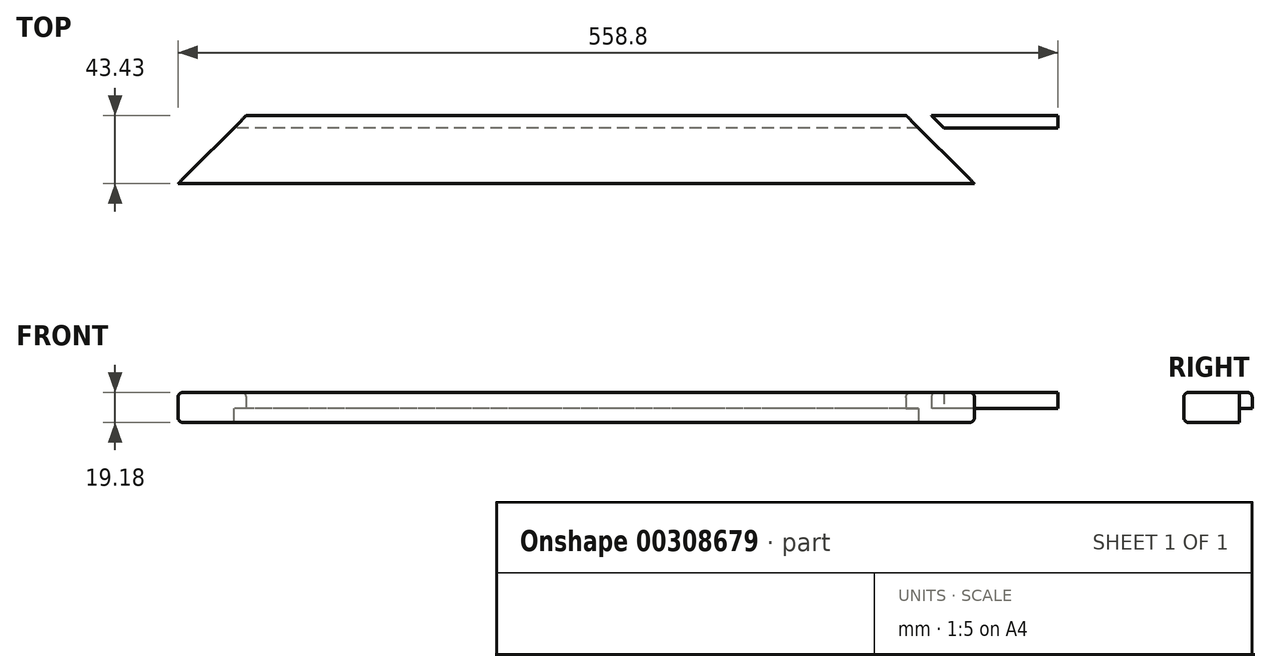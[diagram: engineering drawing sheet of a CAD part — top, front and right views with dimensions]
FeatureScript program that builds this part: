
annotation { "Feature Type Name" : "Feature", "Feature Type Description" : "" }
export const myFeature = defineFeature(function(context is Context, id is Id, definition is map)
    precondition{}
    {
        {
            var Q0;
            Q0=qCreatedBy(makeId("Right.planeOp"),FACE);
            var sketch = newSketch(context, id + "F0", { "sketchPlane" : qUnion([Q0])});
            skLineSegment(sketch, "E0.bottom", {"start": v(-48.17, 35.19) * mm, "end": v(-11.09, 35.19) * mm});
            skLineSegment(sketch, "E0.top", {"start": v(-48.17, 16) * mm, "end": v(-15.91, 16) * mm});
            skLineSegment(sketch, "E0.left", {"start": v(-51.34, 32.01) * mm, "end": v(-51.34, 19.18) * mm});
            skLineSegment(sketch, "E0.right", {"start": v(-7.91, 32.01) * mm, "end": v(-7.91, 24.9) * mm});
            skPoint(sketch, "E1.visualSharp", {"position": v(-51.34, 35.19) * mm});
            skArc(sketch, "E1.filletArc", {"start": v(-48.17, 35.19) * mm, "mid": v(-50.41, 34.26) * mm, "end": v(-51.34, 32.01) * mm});
            skPoint(sketch, "E2.visualSharp", {"position": v(-51.34, 16) * mm});
            skArc(sketch, "E2.filletArc", {"start": v(-51.34, 19.18) * mm, "mid": v(-50.41, 16.94) * mm, "end": v(-48.17, 16) * mm});
            skPoint(sketch, "E3.visualSharp", {"position": v(-7.91, 35.19) * mm});
            skArc(sketch, "E3.filletArc", {"start": v(-7.91, 32.01) * mm, "mid": v(-8.84, 34.26) * mm, "end": v(-11.09, 35.19) * mm});
            skLineSegment(sketch, "E4", {"start": v(-15.91, 24.9) * mm, "end": v(-15.91, 16) * mm});
            skLineSegment(sketch, "E5", {"start": v(-7.91, 24.9) * mm, "end": v(-15.91, 24.9) * mm});
            skSolve(sketch);
        }
        {
            var Q0;
            Q0=makeQuery(id+"F0.imprint","IMPRINT",FACE,{"disambiguationData":[TD([[makeQuery(id+"F0.imprint","IMPRINT",EDGE,{"derivedFrom":sQuery(id+"F0.wireOp",EDGE,"E0.bottom")}),-1.0]])]});
            extrude(context, id + "F1", {"entities" : qUnion([Q0]), "depth" : 558.8 * mm});
        }
        {
            var Q0;
            Q0=makeQuery(id+"F1.opExtrude","SWEPT_FACE",FACE,{"disambiguationData":[OSD([sQuery(id+"F0.wireOp",EDGE,"E0.bottom")])]});
            var sketch = newSketch(context, id + "F2", { "sketchPlane" : qUnion([Q0])});
            skLineSegment(sketch, "E6.0", {"start": v(558.8, -51.34) * mm, "end": v(0, -51.34) * mm});
            skLineSegment(sketch, "E7", {"start": v(0, -51.34) * mm, "end": v(43.43, -7.91) * mm});
            skLineSegment(sketch, "E8.0", {"start": v(558.8, -7.91) * mm, "end": v(0, -7.91) * mm});
            skLineSegment(sketch, "E9", {"start": v(0, -51.34) * mm, "end": v(0, -7.91) * mm});
            skSolve(sketch);
        }
        {
            var Q0;
            {var subQ0=sQuery(id+"F2.wireOp",EDGE,"E8.0");var subQ1=sQuery(id+"F2.wireOp",EDGE,"E7");var subQ2=makeQuery(id+"F2.imprint","INTERSECT",VERTEX,{"derivedFrom":[subQ1,subQ0]});Q0=makeQuery(id+"F2.imprint","IMPRINT",FACE,{"disambiguationData":[TD([[makeQuery(id+"F2.imprint","IMPRINT",EDGE,{"disambiguationData":[TD([[subQ2,-1.0]])],"derivedFrom":subQ0}),1.0]])]});}
            var Q1;
            {var subQ0=sQuery(id+"F2.wireOp",EDGE,"E7");var subQ1=sQuery(id+"F0.wireOp",EDGE,"E0.bottom");var subQ2=makeQuery(id+"F1.opExtrude","SWEPT_EDGE",EDGE,{"disambiguationData":[OSD([subQ1,sQuery(id+"F0.wireOp",EDGE,"E1.filletArc")])]});var subQ3=makeQuery(id+"F2.imprint","INTERSECT",VERTEX,{"derivedFrom":[subQ2,subQ0]});Q1=makeQuery(id+"F2.imprint","IMPRINT",FACE,{"disambiguationData":[TD([[makeQuery(id+"F2.imprint","IMPRINT",EDGE,{"disambiguationData":[TD([[subQ3,-1.0]])],"derivedFrom":subQ0}),1.0]])]});}
            var Q2;
            {var subQ0=sQuery(id+"F2.wireOp",EDGE,"E9");var subQ1=sQuery(id+"F2.wireOp",EDGE,"E7");var subQ2=makeQuery(id+"F2.imprint","INTERSECT",VERTEX,{"derivedFrom":[subQ1,subQ0]});Q2=makeQuery(id+"F2.imprint","IMPRINT",FACE,{"disambiguationData":[TD([[makeQuery(id+"F2.imprint","IMPRINT",EDGE,{"disambiguationData":[TD([[subQ2,-1.0]])],"derivedFrom":subQ1}),1.0]])]});}
            extrude(context, id + "F3", {"entities" : qUnion([Q0, Q1, Q2]), "operationType" : NewBodyOperationType.REMOVE, "endBound" : BoundingType.THROUGH_ALL, "oppositeDirection" : true, "depth" : 25.4 * mm});
        }
        {
            var Q0;
            Q0=makeQuery(id+"F1.opExtrude","SWEPT_FACE",FACE,{"disambiguationData":[OSD([sQuery(id+"F0.wireOp",EDGE,"E0.top")])]});
            var sketch = newSketch(context, id + "F4", { "sketchPlane" : qUnion([Q0])});
            skLineSegment(sketch, "E10.0", {"start": v(558.8, 51.34) * mm, "end": v(0, 51.34) * mm});
            skLineSegment(sketch, "E11.0", {"start": v(558.8, 7.91) * mm, "end": v(43.43, 7.91) * mm});
            skLineSegment(sketch, "E12", {"start": v(478.4, 51.34) * mm, "end": v(478.4, -40.2) * mm});
            skLineSegment(sketch, "E13", {"start": v(478.4, 7.91) * mm, "end": v(521.84, 51.34) * mm});
            skLineSegment(sketch, "E14.0", {"start": v(558.8, 48.17) * mm, "end": v(558.8, 15.91) * mm});
            skPoint(sketch, "E15.0", {"position": v(558.8, 50.41) * mm});
            skLineSegment(sketch, "E16.0", {"start": v(558.8, 7.91) * mm, "end": v(558.8, 15.91) * mm});
            skLineSegment(sketch, "E17", {"start": v(521.84, 51.34) * mm, "end": v(558.8, 51.34) * mm});
            skLineSegment(sketch, "E18", {"start": v(558.8, 7.91) * mm, "end": v(478.4, 7.91) * mm});
            skLineSegment(sketch, "E19", {"start": v(558.8, 51.34) * mm, "end": v(558.8, 7.91) * mm});
            skLineSegment(sketch, "E20.0", {"start": v(558.8, 15.91) * mm, "end": v(35.43, 15.91) * mm});
            skLineSegment(sketch, "E21", {"start": v(35.43, 15.91) * mm, "end": v(35.43, -67.97) * mm});
            skSolve(sketch);
        }
        {
            var Q0;
            {var subQ0=sQuery(id+"F4.wireOp",EDGE,"E17");Q0=makeQuery(id+"F4.imprint","IMPRINT",FACE,{"disambiguationData":[TD([[makeQuery(id+"F4.imprint","IMPRINT",EDGE,{"derivedFrom":subQ0}),-1.0]])]});}
            var Q1;
            {var subQ0=sQuery(id+"F4.wireOp",EDGE,"E13");var subQ1=sQuery(id+"F0.wireOp",EDGE,"E0.top");var subQ2=makeQuery(id+"F1.opExtrude","SWEPT_EDGE",EDGE,{"disambiguationData":[OSD([subQ1,sQuery(id+"F0.wireOp",EDGE,"E4")])]});var subQ3=makeQuery(id+"F4.imprint","INTERSECT",VERTEX,{"derivedFrom":[subQ2,subQ0]});Q1=makeQuery(id+"F4.imprint","IMPRINT",FACE,{"disambiguationData":[TD([[makeQuery(id+"F4.imprint","IMPRINT",EDGE,{"disambiguationData":[TD([[subQ3,-1.0]])],"derivedFrom":subQ0}),-1.0]])]});}
            var Q2;
            {var subQ0=sQuery(id+"F4.wireOp",EDGE,"E18");Q2=makeQuery(id+"F4.imprint","IMPRINT",FACE,{"disambiguationData":[TD([[makeQuery(id+"F4.imprint","IMPRINT",EDGE,{"derivedFrom":subQ0}),-1.0]])]});}
            extrude(context, id + "F5", {"entities" : qUnion([Q0, Q1, Q2]), "operationType" : NewBodyOperationType.REMOVE, "endBound" : BoundingType.THROUGH_ALL, "oppositeDirection" : true, "depth" : 25.4 * mm});
        }
        {
            var Q0;
            Q0=makeQuery(id+"F1.opExtrude","SWEPT_FACE",FACE,{"disambiguationData":[OSD([sQuery(id+"F0.wireOp",EDGE,"E0.top")])]});
            var sketch = newSketch(context, id + "F6", { "sketchPlane" : qUnion([Q0])});
            skLineSegment(sketch, "E22", {"start": v(35.43, 15.91) * mm, "end": v(35.43, -96.8) * mm});
            skLineSegment(sketch, "E23.0", {"start": v(470.4, 15.53) * mm, "end": v(470.4, -96.8) * mm});
            skLineSegment(sketch, "E24.0", {"start": v(521.84, 51.34) * mm, "end": v(0, 51.34) * mm});
            skLineSegment(sketch, "E25", {"start": v(470.4, 14.7) * mm, "end": v(470.4, 15.91) * mm});
            skLineSegment(sketch, "E26", {"start": v(462.4, 7.91) * mm, "end": v(507.73, 53.23) * mm});
            skLineSegment(sketch, "E27.0", {"start": v(478.4, 7.91) * mm, "end": v(43.43, 7.91) * mm});
            skPoint(sketch, "E28.0", {"position": v(482.4, 11.91) * mm});
            skLineSegment(sketch, "E29.0", {"start": v(478.4, 7.91) * mm, "end": v(486.41, 15.91) * mm});
            skLineSegment(sketch, "E30.0", {"start": v(486.41, 15.91) * mm, "end": v(518.67, 48.17) * mm});
            skPoint(sketch, "E30.1", {"position": v(520.72, 50.22) * mm});
            skLineSegment(sketch, "E31.0", {"start": v(521.84, 51.34) * mm, "end": v(518.67, 48.17) * mm});
            skSolve(sketch);
        }
        {
            var Q0;
            {var subQ0=sQuery(id+"F6.wireOp",EDGE,"E31.0");Q0=makeQuery(id+"F6.imprint","IMPRINT",FACE,{"disambiguationData":[TD([[makeQuery(id+"F6.imprint","IMPRINT",EDGE,{"derivedFrom":subQ0}),-1.0]])]});}
            var Q1;
            {var subQ4=sQuery(id+"F6.wireOp",EDGE,"E29.0");Q1=makeQuery(id+"F6.imprint","IMPRINT",FACE,{"disambiguationData":[TD([[makeQuery(id+"F6.imprint","IMPRINT",EDGE,{"derivedFrom":subQ4}),1.0]])]});}
            var Q2;
            {var subQ1=sQuery(id+"F6.wireOp",EDGE,"E25");var subQ5=makeQuery(id+"F6.imprint","IMPRINT",VERTEX,{"derivedFrom":subQ1});Q2=makeQuery(id+"F6.imprint","IMPRINT",FACE,{"disambiguationData":[TD([[makeQuery(id+"F6.imprint","IMPRINT",EDGE,{"disambiguationData":[TD([[subQ5,1.0]])],"derivedFrom":subQ1}),1.0]])]});}
            var Q3;
            {var subQ6=sQuery(id+"F6.wireOp",EDGE,"E30.0");Q3=makeQuery(id+"F6.imprint","IMPRINT",FACE,{"disambiguationData":[TD([[makeQuery(id+"F6.imprint","IMPRINT",EDGE,{"derivedFrom":subQ6}),1.0]])]});}
            extrude(context, id + "F7", {"entities" : qUnion([Q0, Q1, Q2, Q3]), "operationType" : NewBodyOperationType.REMOVE, "endBound" : BoundingType.THROUGH_ALL, "oppositeDirection" : true, "depth" : 25.4 * mm});
        }
    });
